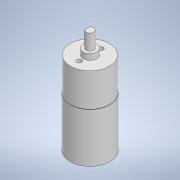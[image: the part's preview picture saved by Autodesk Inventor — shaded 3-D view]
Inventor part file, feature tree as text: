
AUTODESK INVENTOR PART (.ipt)
format: ipt  version: 2022 (Build 260153000, 153)  size: 136,704 bytes
history: native  units: mm
features: extrude x6, sketch x6, projected_geometry x1
ambient origin geometry x8: Origin, YZ Plane, XZ Plane, XY Plane, X Axis, Y Axis, Z Axis, Center Point
bodies: Solid1 (feature_tree)
feature tree (13):
  extrude  "Extrusion1"  Depth=25.1mm TaperAngle=0.0deg
  extrude  "Extrusion2"  Depth=17.0mm TaperAngle=0.0deg
  extrude  "Extrusion3"  Depth=3.0mm TaperAngle=0.0deg
  extrude  "Extrusion4"  Depth=8.0mm TaperAngle=0.0deg
  extrude  "Extrusion5"  Depth=7.0mm TaperAngle=0.0deg
  extrude  "Extrusion6"  Depth=11.0mm
  sketch  "Sketch1"  dims[d0=20.4mm d1=25.1mm d2=0.0mm]
  sketch  "Sketch2"  dims[d3=20.0mm d4=17.0mm d5=0.0mm]
  sketch  "Sketch3"  dims[d6=7.0mm d7=3.0mm d8=0.0mm]
  sketch  "Sketch4"  dims[d9=4.0mm d10=8.0mm d11=0.0mm]
  sketch  "Sketch5"  dims[d12=0.5mm d13=7.0mm d14=0.0mm]
  projected_geometry  "Projected Loop1"
  sketch  "Sketch6"  dims[d15=2.5mm d16=11.0mm d17=10.0mm d18=0.0mm]
